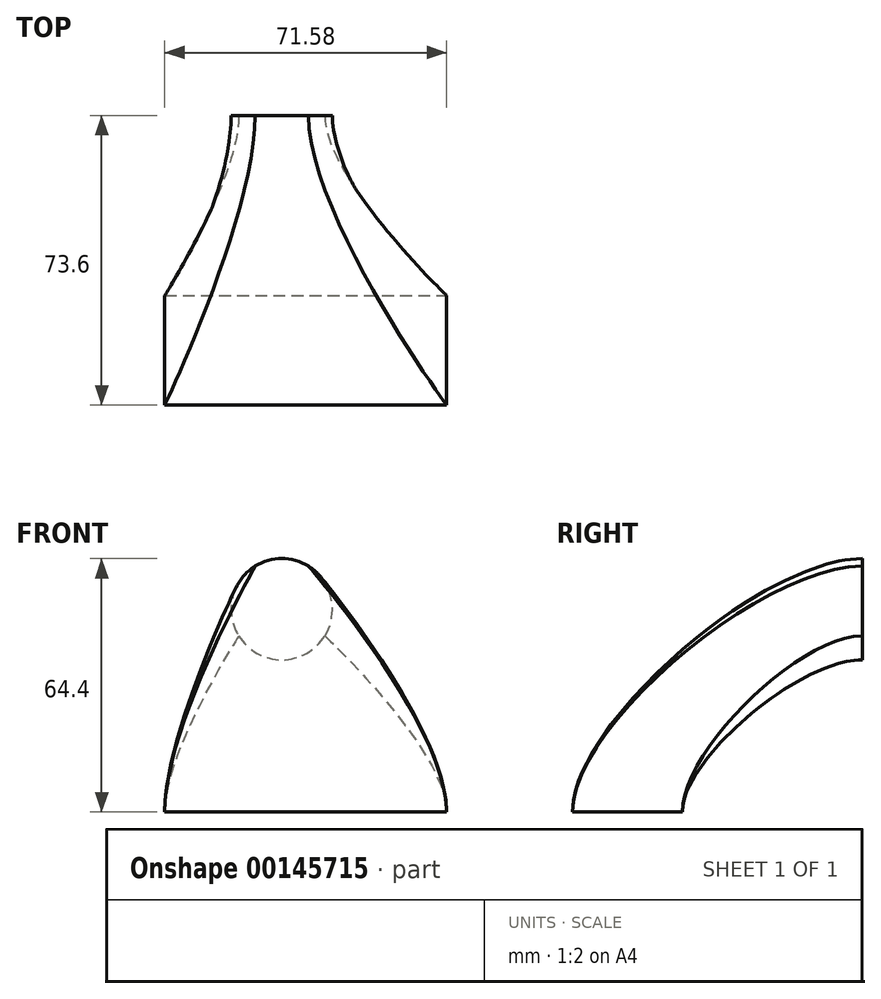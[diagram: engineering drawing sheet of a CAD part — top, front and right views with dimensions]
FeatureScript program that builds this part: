
annotation { "Feature Type Name" : "Feature", "Feature Type Description" : "" }
export const myFeature = defineFeature(function(context is Context, id is Id, definition is map)
    precondition{}
    {
        {
            var Q0;
            Q0=qCreatedBy(makeId("Front.planeOp"),FACE);
            var sketch = newSketch(context, id + "F0", { "sketchPlane" : qUnion([Q0])});
            skArc(sketch, "E0", {"start": v(6.78, 62.47) * mm, "mid": v(0, 64.4) * mm, "end": v(-6.78, 62.47) * mm});
            skArc(sketch, "E1", {"start": v(10.93, 44.76) * mm, "mid": v(12.52, 54.48) * mm, "end": v(6.78, 62.47) * mm});
            skArc(sketch, "E2", {"start": v(-6.78, 62.47) * mm, "mid": v(-12.52, 54.48) * mm, "end": v(-10.93, 44.76) * mm});
            skArc(sketch, "E3", {"start": v(-10.93, 44.76) * mm, "mid": v(0, 38.68) * mm, "end": v(10.93, 44.76) * mm});
            skSolve(sketch);
        }
        {
            var Q0;
            Q0=qCreatedBy(makeId("Top.planeOp"),FACE);
            var sketch = newSketch(context, id + "F1", { "sketchPlane" : qUnion([Q0])});
            skLineSegment(sketch, "E4.bottom", {"start": v(-29.73, -73.6) * mm, "end": v(41.85, -73.6) * mm});
            skLineSegment(sketch, "E4.top", {"start": v(-29.73, -45.72) * mm, "end": v(41.85, -45.72) * mm});
            skLineSegment(sketch, "E4.left", {"start": v(-29.73, -73.6) * mm, "end": v(-29.73, -45.72) * mm});
            skLineSegment(sketch, "E4.right", {"start": v(41.85, -73.6) * mm, "end": v(41.85, -45.72) * mm});
            skSolve(sketch);
        }
        {
            var Q0;
            Q0=qSketchRegion(id+"F0",true);
            var Q1;
            Q1=qSketchRegion(id+"F1",true);
            var Q2;
            Q2=sQuery(id+"F1.wireOp",VERTEX,"E4.right.end");
            var Q3;
            Q3=sQuery(id+"F0.wireOp",VERTEX,"E3.end");
            loft(context, id + "F2", {"startCondition" : LoftEndDerivativeType.NORMAL_TO_PROFILE, "startMagnitude" : 1, "endCondition" : LoftEndDerivativeType.NORMAL_TO_PROFILE, "endMagnitude" : 1, "sheetProfilesArray" : [{ "sheetProfileEntities" : qUnion([Q0]) }, { "sheetProfileEntities" : qUnion([Q1]) }], "connections" : [{ "connectionEntities" : qUnion([Q2, Q3]), "connectionEdgeQueries" : qUnion([]), "connectionEdgeParameters" : [] }]});
        }
    });
